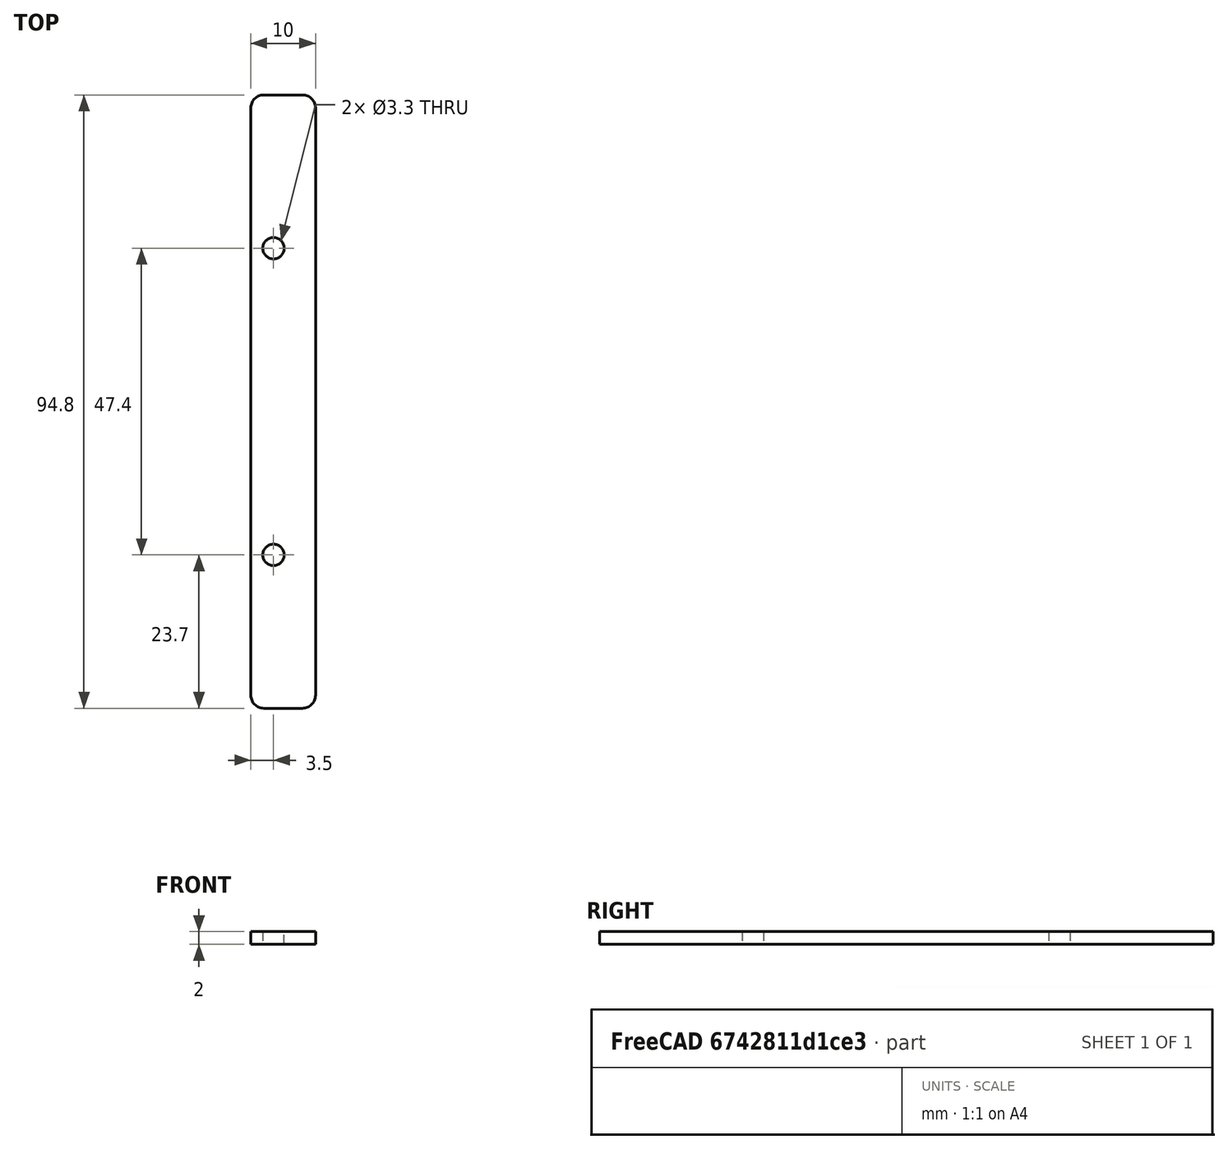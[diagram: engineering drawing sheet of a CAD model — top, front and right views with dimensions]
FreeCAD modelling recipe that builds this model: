
FCSTD DOCUMENT  (FreeCAD 1.0R39285 (Git))
Label: pupae_thermal_device_cover
License: All rights reserved
LicenseURL: https://en.wikipedia.org/wiki/All_rights_reserved
objects: Spreadsheet::Sheet×1, Sketcher::SketchObject×1, PartDesign::Pad×1, PartDesign::Body×1
note: 6 computed .brp shape members not serialized (recipe doc carries the construction recipe); baked Part::Feature solids carry a one-line shape summary decoded from their .brp
EXTERNAL_REF file=pupae_thermal_device_frame.FCStd obj=Spreadsheet

FEATURE [Spreadsheet::Sheet] Spreadsheet
  cells = A2='Design Parameters; A3='cover_thickness; B3(cover_thickness)==2 mm; A4='cover_overlap; B4(cover_overlap)==3 mm; A5='wall_thickness; B5(wall_thickness)==pupae_thermal_device_frame#Spreadsheet.wall_thickness; A6='base_outside_length; B6(base_outside_length)==pupae_thermal_device_frame#Spreadsheet.base_outside_length; A7='base_outside_width; B7(base_outside_width)==pupae_thermal_device_frame#Spreadsheet.base_outside_width; A8='base_outside_corner_fillet_radius; B8(base_outside_corner_fillet_radius)==pupae_thermal_device_frame#Spreadsheet.base_outside_corner_fillet_radius; A9='mount_hole_diameter; B9(mount_hole_diameter)==0.13 in
FEATURE [Sketcher::SketchObject] Sketch  label="CoverSketch"
  ArcFitTolerance = 1e-06
  AttachmentSupport = -> [XY_Plane]
  FullyConstrained = true
  MakeInternals = false
  MapMode = 5
  expr: Constraints[19] = Spreadsheet.base_outside_corner_fillet_radius
  expr: Constraints[21] = Spreadsheet.base_outside_length
  expr: Constraints[22] = Spreadsheet.wall_thickness
  expr: Constraints[36] = Spreadsheet.cover_overlap
  expr: Constraints[57] = Spreadsheet.mount_hole_diameter
  sketch-geometry (26):
    g0: LineSegment StartX=-3.5 StartY=45.4 StartZ=0 EndX=-3.5 EndY=-45.4 EndZ=0
    g1: LineSegment StartX=-1.5 StartY=-47.4 StartZ=0 EndX=1.5 EndY=-47.4 EndZ=0
    g2: LineSegment [constr] StartX=3.5 StartY=-45.4 StartZ=0 EndX=3.5 EndY=45.4 EndZ=0
    g3: LineSegment StartX=1.5 StartY=47.4 StartZ=0 EndX=-1.5 EndY=47.4 EndZ=0
    g4: ArcOfCircle CenterX=-1.5 CenterY=45.4 CenterZ=0 NormalX=0 NormalY=0 NormalZ=1 AngleXU=0 Radius=2 StartAngle=1.5708 EndAngle=3.14159
    g5: ArcOfCircle CenterX=-1.5 CenterY=-45.4 CenterZ=0 NormalX=0 NormalY=0 NormalZ=1 AngleXU=0 Radius=2 StartAngle=3.14159 EndAngle=4.71239
    g6: ArcOfCircle [constr] CenterX=1.5 CenterY=-45.4 CenterZ=0 NormalX=0 NormalY=0 NormalZ=1 AngleXU=0 Radius=2 StartAngle=4.71239 EndAngle=6.28319
    g7: ArcOfCircle [constr] CenterX=1.5 CenterY=45.4 CenterZ=0 NormalX=0 NormalY=0 NormalZ=1 AngleXU=0 Radius=2 StartAngle=6e-16 EndAngle=1.5708
    g8: GeomPoint [constr] X=-3.5 Y=47.4 Z=0
    g9: GeomPoint [constr] X=3.5 Y=-47.4 Z=0
    g10: LineSegment StartX=1.5 StartY=-47.4 StartZ=0 EndX=3.5 EndY=-47.4 EndZ=0
    g11: LineSegment StartX=1.5 StartY=47.4 StartZ=0 EndX=3.5 EndY=47.4 EndZ=0
    g12: LineSegment [constr] StartX=3.5 StartY=45.4 StartZ=0 EndX=3.5 EndY=47.4 EndZ=0
    g13: LineSegment [constr] StartX=3.5 StartY=47.4 StartZ=0 EndX=6.5 EndY=47.4 EndZ=0
    g14: LineSegment [constr] StartX=3.5 StartY=-47.4 StartZ=0 EndX=6.5 EndY=-47.4 EndZ=0
    g15: LineSegment [constr] StartX=6.5 StartY=47.4 StartZ=0 EndX=6.5 EndY=-47.4 EndZ=0
    g16: ArcOfCircle CenterX=4.5 CenterY=-45.4 CenterZ=0 NormalX=0 NormalY=0 NormalZ=1 AngleXU=0 Radius=2 StartAngle=4.71238 EndAngle=6.28319
    g17: ArcOfCircle CenterX=4.5 CenterY=45.4 CenterZ=0 NormalX=0 NormalY=0 NormalZ=1 AngleXU=0 Radius=2 StartAngle=6e-16 EndAngle=1.5708
    g18: LineSegment StartX=3.5 StartY=47.4 StartZ=0 EndX=4.5 EndY=47.4 EndZ=0
    g19: LineSegment StartX=6.5 StartY=45.4 StartZ=0 EndX=6.5 EndY=-45.4 EndZ=0
    g20: LineSegment StartX=4.49999 StartY=-47.4 StartZ=0 EndX=3.5 EndY=-47.4 EndZ=0
    g21: LineSegment [constr] StartX=0 StartY=47.4 StartZ=0 EndX=0 EndY=-47.4 EndZ=0
    g22: GeomPoint [constr] X=0 Y=23.7 Z=0
    g23: GeomPoint [constr] X=0 Y=-23.7 Z=0
    g24: Circle CenterX=0 CenterY=23.7 CenterZ=0 NormalX=0 NormalY=0 NormalZ=1 AngleXU=0 Radius=1.651
    g25: Circle CenterX=0 CenterY=-23.7 CenterZ=0 NormalX=0 NormalY=0 NormalZ=1 AngleXU=0 Radius=1.651
  constraints (58):
    c: Tangent(g0,g4) = -1.5708
    c: Tangent(g0,g5) = -1.5708
    c: Tangent(g1,g5) = -1.5708
    c: Tangent(g1,g6) = -1.5708
    c: Tangent(g2,g6) = -1.5708
    c: Tangent(g2,g7) = -1.5708
    c: Tangent(g3,g7) = -1.5708
    c: Tangent(g3,g4) = -1.5708
    c: Vertical(g0)
    c: Vertical(g2)
    c: Horizontal(g1)
    c: Horizontal(g3)
    c: Equal(g4,g5)
    c: Equal(g5,g6)
    c: Equal(g6,g7)
    c: PointOnObject(g8,g0)
    c: PointOnObject(g8,g3)
    c: PointOnObject(g9,g1)
    c: PointOnObject(g9,g2)
    c: Radius(g5) = 2
    c: Symmetric(g4,g6,g-1)
    c: DistanceY(g1,g3) = 94.8
    c: Distance(g0,g2) = 7
    c: Coincident(g10,g1)
    c: Coincident(g10,g9)
    c: Coincident(g11,g3)
    c: Horizontal(g11)
    c: Coincident(g12,g11)
    c: Vertical(g12)
    c: Coincident(g2,g12)
    c: Coincident(g13,g11)
    c: Horizontal(g13)
    c: Coincident(g14,g9)
    c: Equal(g14,g13)
    c: Coincident(g15,g13)
    c: Coincident(g15,g14)
    c: DistanceX(g14,g14) = 3
    c: Tangent(g16,g15) = 1.5708
    c: Tangent(g16,g14) = -1.5708
    c: Equal(g16,g6)
    c: Tangent(g17,g13) = 1.5708
    c: Tangent(g17,g15) = 1.5708
    c: Equal(g17,g7)
    c: Coincident(g18,g11)
    c: Coincident(g18,g17)
    c: Coincident(g19,g17)
    c: Tangent(g19,g16) = 1.5708
    c: Vertical(g19)
    c: Coincident(g20,g9)
    c: Coincident(g20,g16)
    c: Symmetric(g3,g3,g21)
    c: Symmetric(g1,g1,g21)
    c: Symmetric(g-1,g21,g22)
    c: Symmetric(g-1,g21,g23)
    c: Coincident(g24,g22)
    c: Coincident(g25,g23)
    c: Equal(g25,g24)
    c: Diameter(g25) = 3.302
FEATURE [PartDesign::Pad] Pad  label="CoverPad"
  Direction = (0,0,1)
  Length = 2
  Length2 = 10
  Profile = -> Sketch
  ReferenceAxis = -> Sketch [N_Axis]
  Refine = true
  Suppressed = false
  Type = 0
  expr: Length = Spreadsheet.cover_thickness
FEATURE [PartDesign::Body] Body
  AllowCompound = false
  Group = -> [Sketch,Pad]
  Origin = -> Origin
  Tip = -> Pad
